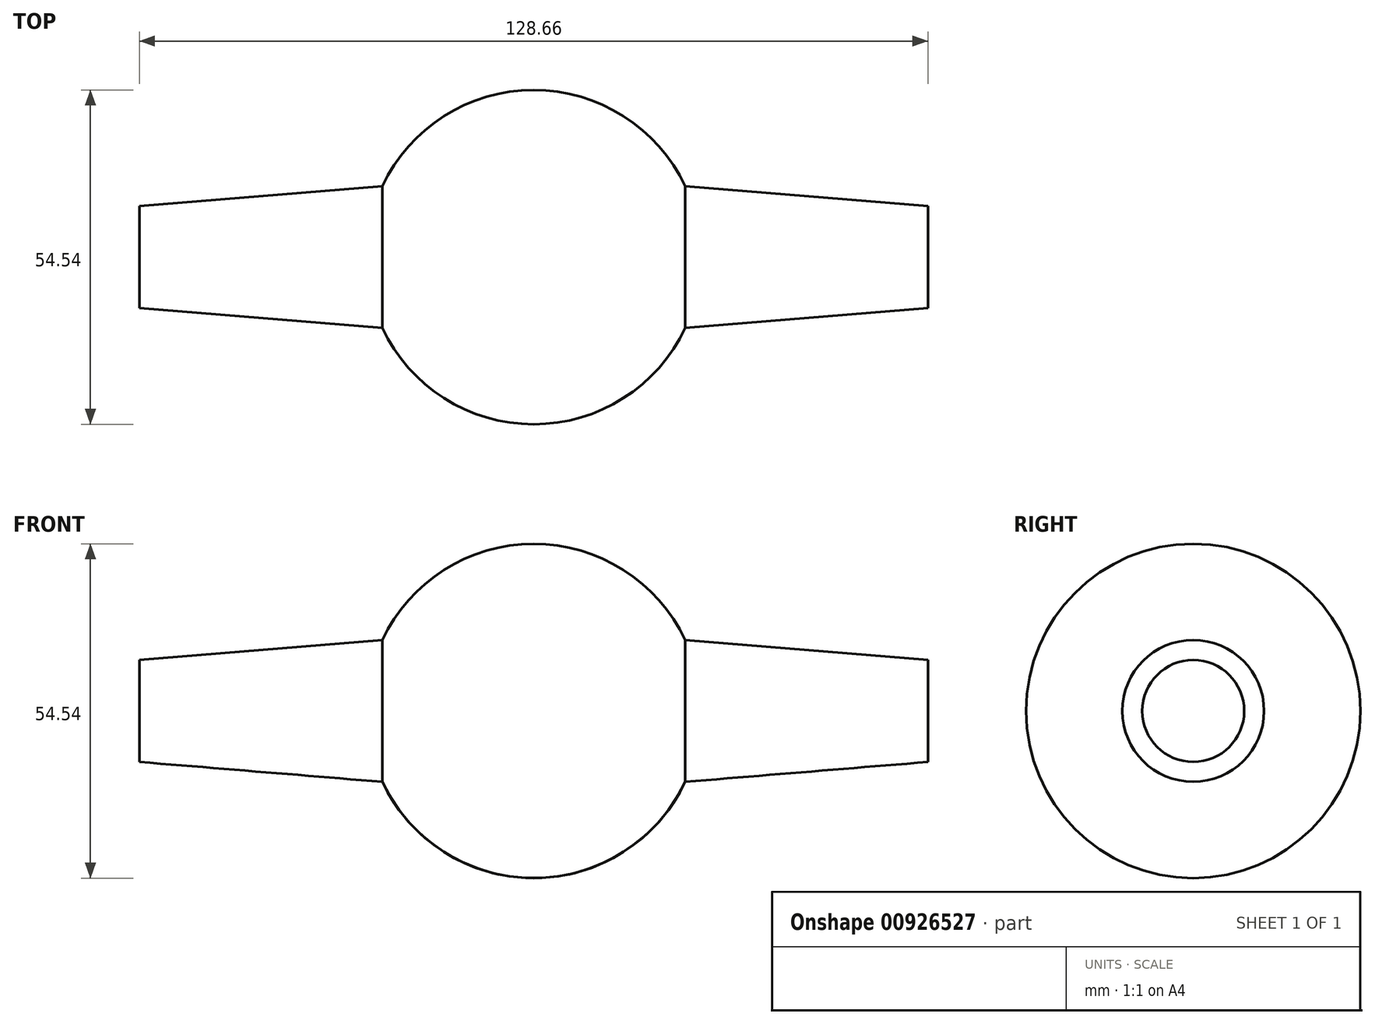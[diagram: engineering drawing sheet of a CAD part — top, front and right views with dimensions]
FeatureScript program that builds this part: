
annotation { "Feature Type Name" : "Feature", "Feature Type Description" : "" }
export const myFeature = defineFeature(function(context is Context, id is Id, definition is map)
    precondition{}
    {
        {
            var Q0;
            Q0=qCreatedBy(makeId("Front.planeOp"),FACE);
            var sketch = newSketch(context, id + "F0", { "sketchPlane" : qUnion([Q0])});
            skArc(sketch, "E0", {"start": v(-24.7, -11.56) * mm, "mid": v(-14.63, -23) * mm, "end": v(0, -27.27) * mm});
            skLineSegment(sketch, "E1", {"start": v(0, 0) * mm, "end": v(-64.33, 0) * mm});
            skLineSegment(sketch, "E2", {"start": v(-64.33, 0) * mm, "end": v(-64.33, -8.32) * mm});
            skLineSegment(sketch, "E3", {"start": v(-64.33, -8.32) * mm, "end": v(-24.7, -11.56) * mm});
            skPoint(sketch, "E4.orphan", {"position": v(0, -13.58) * mm});
            skLineSegment(sketch, "E5", {"start": v(0, 0) * mm, "end": v(0, -27.27) * mm});
            skSolve(sketch);
        }
        {
            var Q0;
            Q0 = qSketchRegion(id + "F0", true);
            var Q1;
            Q1=sQuery(id+"F0.wireOp",EDGE,"E1");
            revolve(context, id + "F1", {"surfaceOperationType" : NewSurfaceOperationType.NEW, "entities" : qUnion([Q0]), "axis" : qUnion([Q1]), "revolveType" : RevolveType.FULL});
        }
        {
            var Q0;
            Q0=makeQuery(id+"F1.opRevolve","SWEPT_BODY",BODY,{"disambiguationData":[OSD([sQuery(id+"F0.wireOp",EDGE,"E0"),sQuery(id+"F0.wireOp",EDGE,"E1"),sQuery(id+"F0.wireOp",EDGE,"E2"),sQuery(id+"F0.wireOp",EDGE,"E3"),sQuery(id+"F0.wireOp",EDGE,"E5")])]});
            var Q1;
            Q1=qCreatedBy(makeId("Right.planeOp"),FACE);
            mirror(context, id + "F2", {"operationType" : NewBodyOperationType.ADD, "entities" : qUnion([Q0]), "mirrorPlane" : qUnion([Q1])});
        }
    });
